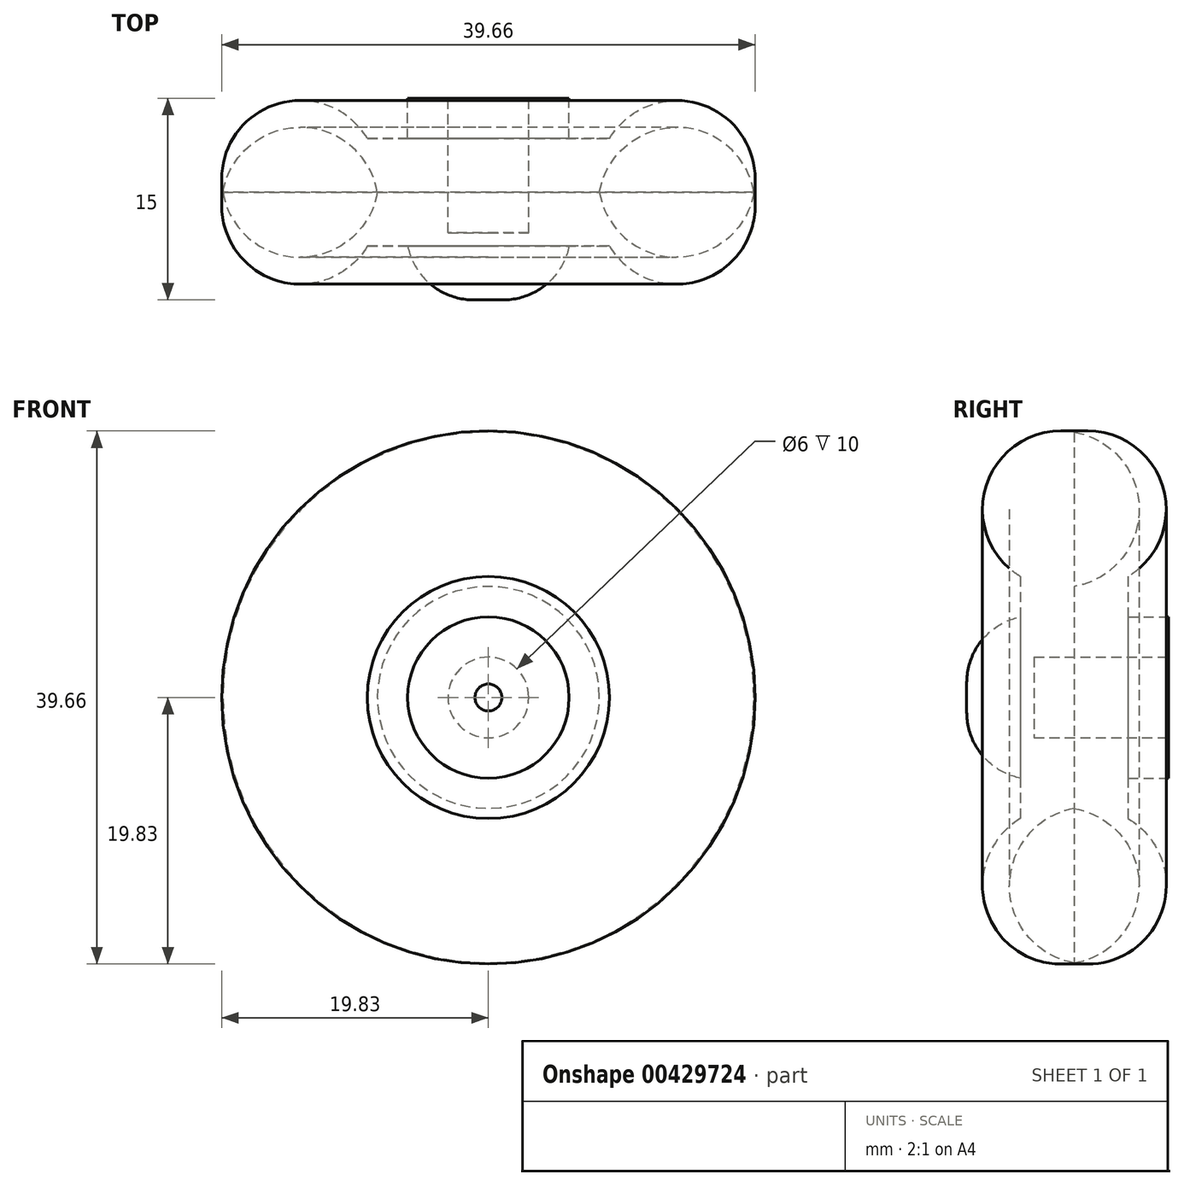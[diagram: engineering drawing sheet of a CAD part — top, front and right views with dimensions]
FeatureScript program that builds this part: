
annotation { "Feature Type Name" : "Feature", "Feature Type Description" : "" }
export const myFeature = defineFeature(function(context is Context, id is Id, definition is map)
    precondition{}
    {
        {
            var Q0;
            Q0=qCreatedBy(makeId("Right.planeOp"),FACE);
            var sketch = newSketch(context, id + "F0", { "sketchPlane" : qUnion([Q0])});
            skLineSegment(sketch, "E0", {"start": v(0, 0) * mm, "end": v(-23.47, 0) * mm, "construction": true});
            skLineSegment(sketch, "E1", {"start": v(0, 0) * mm, "end": v(0, 6) * mm});
            skLineSegment(sketch, "E2", {"start": v(0, 6) * mm, "end": v(-3, 6) * mm});
            skLineSegment(sketch, "E3", {"start": v(-3, 6) * mm, "end": v(-3, 9) * mm});
            skPoint(sketch, "E4", {"position": v(-6, 14) * mm});
            skPoint(sketch, "E5", {"position": v(-8, 14) * mm});
            skArc(sketch, "E6", {"start": v(-7, 19.74) * mm, "mid": v(-5.5, 8.2) * mm, "end": v(-6, 19.83) * mm});
            skArc(sketch, "E7", {"start": v(-8, 19.83) * mm, "mid": v(-8.5, 8.2) * mm, "end": v(-7, 19.74) * mm});
            skLineSegment(sketch, "E8", {"start": v(-8, 19.83) * mm, "end": v(-6, 19.83) * mm});
            skLineSegment(sketch, "E9", {"start": v(-11, 9) * mm, "end": v(-11, 6) * mm});
            skLineSegment(sketch, "E10", {"start": v(-15, 0) * mm, "end": v(-15, 1) * mm});
            skLineSegment(sketch, "E11", {"start": v(-15, 0) * mm, "end": v(0, 0) * mm});
            skPoint(sketch, "E12.orphan", {"position": v(-15, -1) * mm});
            skArc(sketch, "E13", {"start": v(-11, 6) * mm, "mid": v(-13.9, 4.22) * mm, "end": v(-15, 1) * mm});
            skSolve(sketch);
        }
        {
            var Q0;
            Q0 = qSketchRegion(id + "F0", true);
            var Q1;
            Q1=sQuery(id+"F0.wireOp",EDGE,"E0");
            revolve(context, id + "F1", {"entities" : qUnion([Q0]), "axis" : qUnion([Q1]), "revolveType" : RevolveType.FULL});
        }
        {
            var Q0;
            Q0=makeQuery(id+"F1.opRevolve","SWEPT_FACE",FACE,{"disambiguationData":[OSD([sQuery(id+"F0.wireOp",EDGE,"E1")])]});
            var sketch = newSketch(context, id + "F2", { "sketchPlane" : qUnion([Q0])});
            skCircle(sketch, "E14", {"center": v(0, 0) * mm, "radius": 3 * mm});
            skSolve(sketch);
        }
        {
            var Q0;
            Q0 = qSketchRegion(id + "F2", true);
            extrude(context, id + "F3", {"entities" : qUnion([Q0]), "operationType" : NewBodyOperationType.REMOVE, "oppositeDirection" : true, "depth" : 10 * mm});
        }
    });
